# Revit family: Hager-VOLTA-Surface_mounted-IP30-With_Cover-With_DIN-Hosted-DE-de
name_source: partatom
category: Electrical Equipment
units: mm (PartAtom-declared; Revit-internal decimal feet)

## family parameters
Cut with Voids When Loaded = No
Host = Face
Maintain Annotation Orientation = Yes
Panel Configuration = Two Columns, Circuits Across
Part Type = Panelboard
Room Calculation Point = No
Round Connector Dimension = Use Diameter
Shared = No

## types (9) — shared parameters
BC_MODEL_ID = 1547181
BC_OBJECT_ID = 513482
BC_OBJECT_VERSION = #3
Code hager = ADD-EC000214_EU
EF000003 - Montageart = Aufputz
EF000008 - Breite = 305 mm  [stored 1.00066 ft]
EF000024 - UV-beständig = No
EF000049 - Tiefe = 96 mm  [stored 0.314961 ft]
EF000116 - RAL-Nummer = 9010
EF001062 - EMV-Ausführung = No
EF001088 - Anbaumöglichkeit = Yes
EF001134 - DIN-Schiene = Yes
EF002950 - Breite in Teilungseinheiten = 12
EF005474 - Schutzart (IP) = IP30
EF006244 - Transparenter Deckel/Tür = No
EF006306 - Mit Schloss = No
EF009212 - Ausführung Deckel = mit Ausschnitt
ETIM class code = EC000214
ETIM class name = Small distribution board
HG000002-Mit tür = Yes
HG000003-Bereich = VOLTA
HG000005-Dicke = 2 mm  [stored 0.00656168 ft]
HG000006-Flush mounted = No
HG000009-Doppelflügeligen Tür = No
HG000010-Asymmetrische Türen = No
HG000012-Türschwenkwinkel = 90.00°
HG000013-Tür links = No
HG000014-Tür rechts = Yes
HG000015-Sichtbarkeit der Türöffnung = Yes
HG000016-3D-Türsichtbarkeit = Yes
HG000017-Distanz zwischen den Polen = 18 mm  [stored 0.0590551 ft]
HG000060-RAL-number = 9010
HG000099-Onfly Template ID-de-DE = 507532
HGEF0002950-Breite in Teilungseinheiten = 12
Manufacturer = Hager
Name = VOLTA-Surface_mounted-IP30-With_Cover-With_DIN-DE
Name BIM&CO = Electricity
Name hager = ADD_Enclosures_EC000214
Uniformat = Low Tension Service & Dist.
Uniformat code = D501001
zero-valued in all types: Default Elevation, EF000218 - Einbautiefe, EF000846 - Einbaubreite, EF001131 - Innentiefe, HG000007-Anzahl der leeren Spalten

## per-type parameters (varying)
| type | BC_VARIANT_ID | EF000007 - Farbe | EF000040 - Höhe | EF000118 - Mit Montageplatte | EF000266 - Anzahl der Reihen | EF000332 - Einbauhöhe | EF004462 - Art der Schließung | EF015776 - Erdungsklemmenblock | EF015777 - Neutralleiterklemmenblock | EF015941 - Signaldurchlassende Tür | HG000001-Anzahl der Spalten | HG000004-Herstellerreferenz | HG000008-Anzahl der leeren Reihen | HG000011-Leere Reihen von unten | HGEF000266-Anzahl der Reihen |
| VOLTA-Surface_mounted_W305_H515_D96_12_Modular_Spacing-VA36D | 1174299 | weiß | 515 mm  [stored 1.68963 ft] | No | 3 | 0 mm  [stored 0 ft] |  | No | No | No | 1 | VA36D | 0 | No | 3 |
| VOLTA-Surface_mounted_W305_H515_D96_12_Modular_Spacing-VA36RM | 1174300 | weiß | 515 mm  [stored 1.68963 ft] | No | 3 | 0 mm  [stored 0 ft] | sonstige | No | No | No | 1 | VA36RM | 0 | No | 3 |
| VOLTA-Surface_mounted_W305_H515_D96_12_Modular_Spacing-VA36WWH | 1174301 |  | 515 mm  [stored 1.68963 ft] | No | 0 | 0 mm  [stored 0 ft] |  | No | No | No | 0 | VA36WWH | 0 | No | 0 |
| VOLTA-Surface_mounted_W305_H640_D96_12_Modular_Spacing-VA48D | 1174302 | weiß | 640 mm  [stored 2.09974 ft] | No | 4 | 0 mm  [stored 0 ft] |  | No | No | No | 1 | VA48D | 0 | No | 4 |
| VOLTA-Surface_mounted_W305_H765_D96_12_Modular_Spacing-VA602NWH | 1174303 | weiß | 765 mm  [stored 2.50984 ft] | Yes | 5 | 765 mm  [stored 2.50984 ft] | sonstige | Yes | Yes | No | 1 | VA602NWH | 3 | Yes | 5 |
| VOLTA-Surface_mounted_W305_H765_D96_12_Modular_Spacing-VA602WWH | 1174304 | weiß | 765 mm  [stored 2.50984 ft] | Yes | 5 | 765 mm  [stored 2.50984 ft] | sonstige | Yes | Yes | Yes | 1 | VA602WWH | 3 | Yes | 5 |
| VOLTA-Surface_mounted_W305_H765_D96_12_Modular_Spacing-VA603NWH | 1174305 | weiß | 765 mm  [stored 2.50984 ft] | Yes | 5 | 765 mm  [stored 2.50984 ft] | sonstige | Yes | Yes | No | 1 | VA603NWH | 2 | Yes | 5 |
| VOLTA-Surface_mounted_W305_H765_D96_12_Modular_Spacing-VA603WWH | 1174306 | weiß | 765 mm  [stored 2.50984 ft] | Yes | 5 | 765 mm  [stored 2.50984 ft] | sonstige | Yes | Yes | Yes | 1 | VA603WWH | 2 | Yes | 5 |
| VOLTA-Surface_mounted_W305_H765_D96_12_Modular_Spacing-VA60CN | 1174308 | weiß | 765 mm  [stored 2.50984 ft] | No | 5 | 0 mm  [stored 0 ft] |  | Yes | Yes | No | 1 | VA60CN | 0 | No | 5 |

note: column(s) folded — value = type name in every type: Reference

note: [stored X ft] marks values corroborated as IEEE doubles in the binary element streams (Revit-internal decimal feet)

## geometry (parser evidence)
native form markers: Sweep x15
no freeform markers — native parametric forms only
